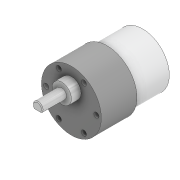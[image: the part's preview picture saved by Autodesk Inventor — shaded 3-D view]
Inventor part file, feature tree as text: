
AUTODESK INVENTOR PART (.ipt)
format: ipt  version: 2022 (Build 260153000, 153)  size: 160,256 bytes
history: native  units: mm
features: sketch x6, extrude x5, projected_geometry x2, chamfer x1, hole x1
ambient origin geometry x8: Origin, YZ Plane, XZ Plane, XY Plane, X Axis, Y Axis, Z Axis, Center Point
bodies: Solid1 (feature_tree)
feature tree (15):
  extrude  "Extrusion1"  Depth=22.0mm TaperAngle=0.0deg
  extrude  "Extrusion2"  Depth=22.0mm TaperAngle=0.0deg
  extrude  "Extrusion3"  Depth=7.0mm
  extrude  "Extrusion4"  Depth=6.0mm
  extrude  "Extrusion5"  Depth=3.0mm
  chamfer  "Chamfer1"  Distance=12.0mm
  hole  "Hole1"  [1 undecoded]
  sketch  "Sketch1"  dims[d0=33.0mm d1=22.0mm d2=0.0mm]
  sketch  "Sketch2"  dims[d4=37.0mm d5=22.0mm d6=0.0mm]
  sketch  "Sketch3"  dims[d7=12.0mm d8=7.0mm]
  sketch  "Sketch4"  dims[d9=6.0mm d10=0.0mm d11=6.0mm]
  sketch  "Sketch5"  dims[d12=3.0mm d13=0.0mm d14=5.2mm d15=12.0mm d16=0.0mm]
  sketch  "Sketch6"  dims[d17=0.5mm d18=2.0mm d19=45.0deg d20=31.0mm d21=30.0mm d23=120.0deg d25=3.2mm d26=6.0mm d27=4.0mm d28=2.0mm d29=90.0deg d30=3.5mm d31=20.594885mm]
  projected_geometry  "Project Cut Edges1"
  projected_geometry  "Project Cut Edges2"
note: 1 required parameter value undecoded (feature->parameter linkage not recoverable at this tier; creation-order binding heuristic only, values carry confidence <= 0.55)
